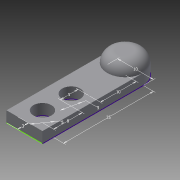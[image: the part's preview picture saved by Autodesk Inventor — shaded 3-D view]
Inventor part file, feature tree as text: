
AUTODESK INVENTOR PART (.ipt)
format: ipt  version: 2015 (Build 190159000, 159)  size: 107,520 bytes
history: native  units: in
note: dims shown in document units (in); Inventor stores cm internally (conversion verified against a paired STEP export)
features: extrude x2, sketch x1, fillet x1
ambient origin geometry x8: Origin, YZ Plane, XZ Plane, XY Plane, X Axis, Y Axis, Z Axis, Center Point
bodies: Body1 (feature_tree)
feature tree (4):
  sketch  "Sketch1"  dims[d0=0.9843in d1=0.3937in d12=0.3937in d13=0.1969in d14=0.1969in d15=0.1181in d16=0.315in d17=0.1969in d18=0.1181in d19=0.0in d20=0.2362in d21=0.0in d22=0.1181in]
  extrude  "Extrusion3"  Depth=0.3937in
  extrude  "Extrusion4"  Depth=0.3937in
  fillet  "Fillet3"  Radius=0.1969in
